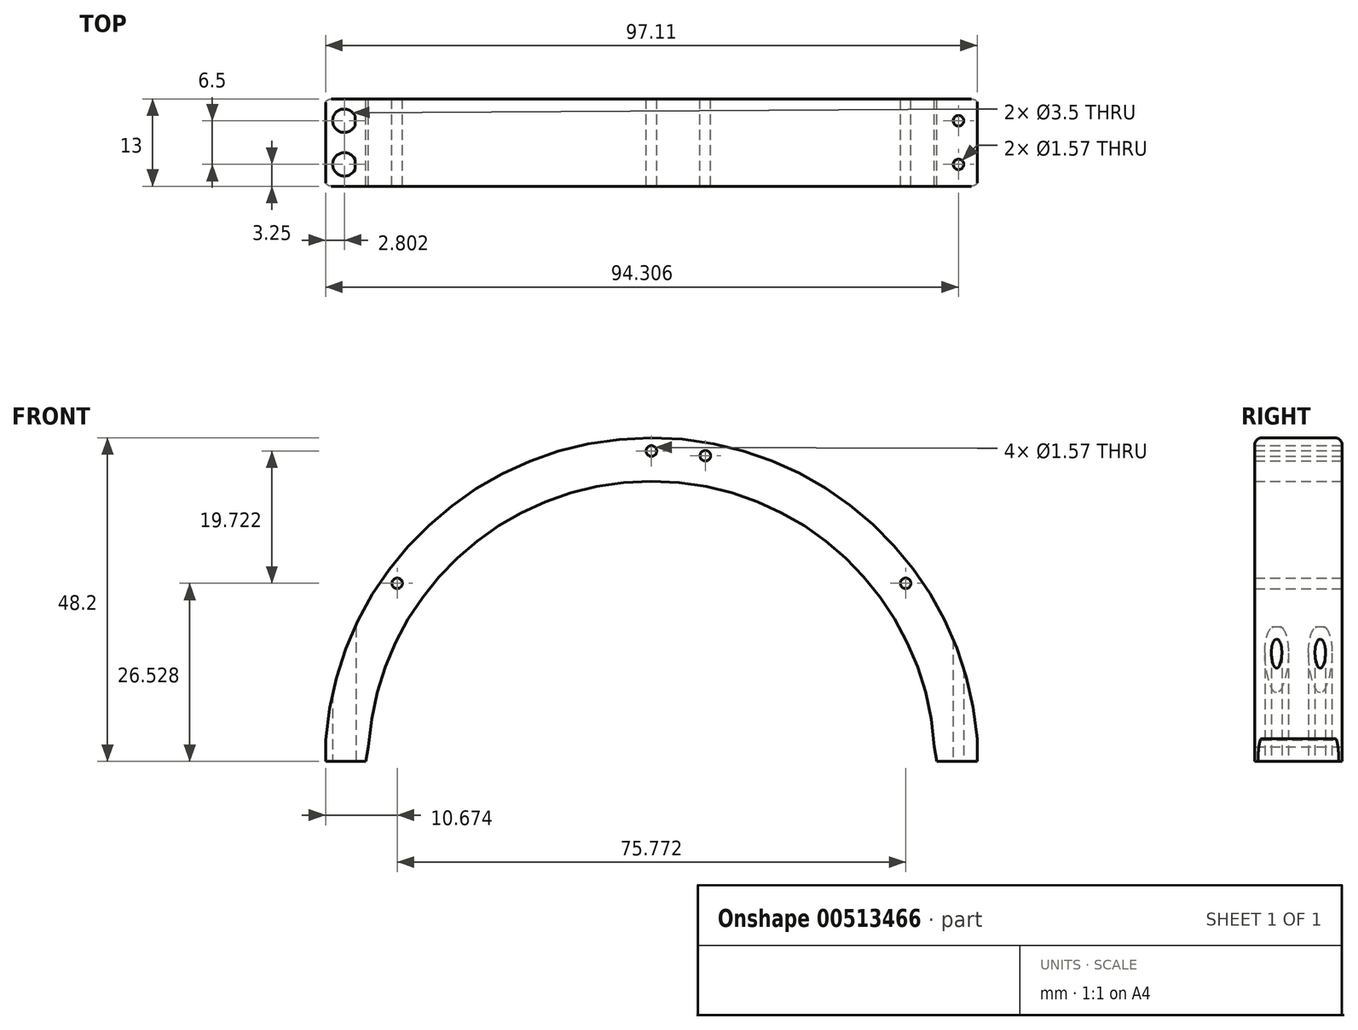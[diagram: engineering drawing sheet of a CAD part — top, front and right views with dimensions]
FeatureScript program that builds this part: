
annotation { "Feature Type Name" : "Feature", "Feature Type Description" : "" }
export const myFeature = defineFeature(function(context is Context, id is Id, definition is map)
    precondition{}
    {
        {
            var Q0;
            Q0=qCreatedBy(makeId("Front.planeOp"),FACE);
            var sketch = newSketch(context, id + "F0", { "sketchPlane" : qUnion([Q0])});
            skLineSegment(sketch, "E0", {"start": v(0, 0) * mm, "end": v(0, 0.5) * mm, "construction": true});
            skLineSegment(sketch, "E1", {"start": v(-42.56, 0.5) * mm, "end": v(-42.56, 2.7) * mm, "construction": true});
            skLineSegment(sketch, "E2", {"start": v(-42.56, 2.7) * mm, "end": v(-34.87, 2.7) * mm, "construction": true});
            skLineSegment(sketch, "E3", {"start": v(-42.56, 0.5) * mm, "end": v(-42.16, 2.7) * mm});
            skLineSegment(sketch, "E4", {"start": v(-42.56, 0.5) * mm, "end": v(0, 0.5) * mm});
            skLineSegment(sketch, "E5.MirrorCS", {"start": v(0.75, 0.5) * mm, "end": v(53.2, 0.5) * mm, "construction": true});
            skLineSegment(sketch, "E6.MirrorCS", {"start": v(-0.5, 0.52) * mm, "end": v(51.96, 0.52) * mm, "construction": true});
            skLineSegment(sketch, "E7", {"start": v(42.05, 0.52) * mm, "end": v(46.75, 0.52) * mm});
            skArc(sketch, "E8", {"start": v(46.25, 0.5) * mm, "mid": v(0, 46.75) * mm, "end": v(-46.25, 0.5) * mm, "construction": true});
            skCircle(sketch, "E9", {"center": v(0, 46.75) * mm, "radius": 1 * mm, "construction": true});
            skLineSegment(sketch, "E10", {"start": v(0, 0.5) * mm, "end": v(9.87, 56.47) * mm, "construction": true});
            skCircle(sketch, "E11", {"center": v(8.03, 46.05) * mm, "radius": 1 * mm, "construction": true});
            skCircle(sketch, "E12", {"center": v(0, 46.75) * mm, "radius": 0.79 * mm, "construction": true});
            skLineSegment(sketch, "E13", {"start": v(0, 0.5) * mm, "end": v(47.68, 33.89) * mm, "construction": true});
            skLineSegment(sketch, "E14", {"start": v(0, 0.5) * mm, "end": v(-44.62, 31.75) * mm, "construction": true});
            skArc(sketch, "E15", {"start": v(42.16, 2.69) * mm, "mid": v(0, 42.25) * mm, "end": v(-42.16, 2.7) * mm});
            skPoint(sketch, "E16.trimOffspring.end.orphan", {"position": v(48.55, 3.87) * mm});
            skArc(sketch, "E17", {"start": v(48.55, 3.87) * mm, "mid": v(-0.08, 48.7) * mm, "end": v(-48.56, 3.71) * mm});
            skLineSegment(sketch, "E18", {"start": v(0, 0) * mm, "end": v(0, 68.97) * mm, "construction": true});
            skPoint(sketch, "E18.endSnap0", {"position": v(0, 0.25) * mm});
            skCircle(sketch, "E19", {"center": v(8.03, 46.05) * mm, "radius": 0.79 * mm, "construction": true});
            skCircle(sketch, "E20", {"center": v(-37.89, 27.03) * mm, "radius": 1 * mm, "construction": true});
            skCircle(sketch, "E21", {"center": v(-37.89, 27.03) * mm, "radius": 0.79 * mm, "construction": true});
            skCircle(sketch, "E22", {"center": v(37.89, 27.03) * mm, "radius": 0.79 * mm, "construction": true});
            skCircle(sketch, "E23", {"center": v(37.89, 27.03) * mm, "radius": 1 * mm, "construction": true});
            skLineSegment(sketch, "E24", {"start": v(48.55, 3.87) * mm, "end": v(48.55, 0.52) * mm});
            skLineSegment(sketch, "E25", {"start": v(48.55, 0.52) * mm, "end": v(46.75, 0.52) * mm});
            skLineSegment(sketch, "E26", {"start": v(-48.56, 3.71) * mm, "end": v(-48.56, 0.5) * mm});
            skLineSegment(sketch, "E27", {"start": v(-42.56, 0.5) * mm, "end": v(-48.56, 0.5) * mm});
            skLineSegment(sketch, "E28.MirrorCS", {"start": v(42.56, 0.5) * mm, "end": v(42.16, 2.7) * mm});
            skSolve(sketch);
        }
        {
            var Q0;
            Q0=makeQuery(id+"F0.imprint","IMPRINT",FACE,{"disambiguationData":[TD([[makeQuery(id+"F0.imprint","IMPRINT",EDGE,{"derivedFrom":sQuery(id+"F0.wireOp",EDGE,"UELqWLm9-NgRF-JSbn-8WNg-CGnTsmN4ftvK")}),1.0]])]});
            var Q1;
            Q1=makeQuery(id+"F0.imprint","IMPRINT",FACE,{"disambiguationData":[TD([[makeQuery(id+"F0.imprint","IMPRINT",EDGE,{"derivedFrom":sQuery(id+"F0.wireOp",EDGE,"E3")}),1.0]])]});
            extrude(context, id + "F1", {"entities" : qUnion([Q0, Q1]), "depth" : 13 * mm, "offsetDistance" : 25 * mm});
        }
        {
            var Q0;
            Q0=sQuery(id+"F0.wireOp",VERTEX,"E9.center");
            var Q1;
            Q1=sQuery(id+"F0.wireOp",VERTEX,"E19.center");
            var Q2;
            Q2=sQuery(id+"F0.wireOp",VERTEX,"E23.center");
            var Q3;
            Q3=sQuery(id+"F0.wireOp",VERTEX,"E21.center");
            var Q4;
            Q4=makeQuery(id+"F1.opExtrude","SWEPT_BODY",BODY,{"disambiguationData":[OSD([sQuery(id+"F0.wireOp",EDGE,"UELqWLm9-NgRF-JSbn-8WNg-CGnTsmN4ftvK"),sQuery(id+"F0.wireOp",EDGE,"zs116KGF-nC6e-KLYb-P88h-iOdVpbJrE8ox"),sQuery(id+"F0.wireOp",EDGE,"E3"),sQuery(id+"F0.wireOp",EDGE,"92af82e9-8861-4be0-b8ea-6b4333b21a260.MirrorCS"),sQuery(id+"F0.wireOp",EDGE,"35d9bae8-f3c6-4467-bb19-02aff46f1e0d0.MirrorCS"),sQuery(id+"F0.wireOp",EDGE,"E7"),sQuery(id+"F0.wireOp",EDGE,"E9"),sQuery(id+"F0.wireOp",EDGE,"E11"),sQuery(id+"F0.wireOp",EDGE,"E15"),sQuery(id+"F0.wireOp",EDGE,"E17"),sQuery(id+"F0.wireOp",EDGE,"E23")])]});
            hole(context, id + "F2", {"style" : HoleStyle.SIMPLE, "endStyle" : HoleEndStyle.BLIND, "oppositeDirection" : true, "holeDiameter" : 1.57 * mm, "holeDepth" : 14.5 * mm, "isTappedThrough" : true, "tappedDepth" : 12 * mm, "tapClearance" : 3, "locations" : qUnion([Q0, Q1, Q2, Q3]), "scope" : qUnion([Q4])});
        }
        {
            var Q0;
            Q0=makeQuery(id+"F1.opExtrude","SWEPT_FACE",FACE,{"disambiguationData":[OSD([sQuery(id+"F0.wireOp",EDGE,"E27")])]});
            var sketch = newSketch(context, id + "F3", { "sketchPlane" : qUnion([Q0])});
            skLineSegment(sketch, "E29.0", {"start": v(-45.76, 14.5) * mm, "end": v(-45.76, 0) * mm, "construction": true});
            skLineSegment(sketch, "E30.0", {"start": v(-42.56, 9.75) * mm, "end": v(-48.36, 9.75) * mm, "construction": true});
            skLineSegment(sketch, "E31.0", {"start": v(-42.56, 3.25) * mm, "end": v(-48.36, 3.25) * mm, "construction": true});
            skCircle(sketch, "E32", {"center": v(-45.76, 9.75) * mm, "radius": 0.48 * mm});
            skCircle(sketch, "E33", {"center": v(-45.76, 3.25) * mm, "radius": 0.56 * mm});
            skSolve(sketch);
        }
        {
            var Q0;
            Q0=sQuery(id+"F3.wireOp",VERTEX,"E32.center");
            var Q1;
            Q1=sQuery(id+"F3.wireOp",VERTEX,"E33.center");
            var Q2;
            Q2=makeQuery(id+"F1.opExtrude","SWEPT_BODY",BODY,{"disambiguationData":[OSD([sQuery(id+"F0.wireOp",EDGE,"E3"),sQuery(id+"F0.wireOp",EDGE,"E7"),sQuery(id+"F0.wireOp",EDGE,"E15"),sQuery(id+"F0.wireOp",EDGE,"E17"),sQuery(id+"F0.wireOp",EDGE,"E24"),sQuery(id+"F0.wireOp",EDGE,"E25"),sQuery(id+"F0.wireOp",EDGE,"E26"),sQuery(id+"F0.wireOp",EDGE,"E27"),sQuery(id+"F0.wireOp",EDGE,"E28.MirrorCS")])]});
            hole(context, id + "F4", {"style" : HoleStyle.SIMPLE, "endStyle" : HoleEndStyle.BLIND, "holeDiameter" : 3.5 * mm, "holeDepth" : 20 * mm, "isTappedThrough" : true, "tappedDepth" : 12 * mm, "tapClearance" : 3, "locations" : qUnion([Q0, Q1]), "scope" : qUnion([Q2])});
        }
        {
            var Q0;
            Q0=makeQuery(id+"F1.opExtrude","SWEPT_FACE",FACE,{"disambiguationData":[OSD([sQuery(id+"F0.wireOp",EDGE,"E7"),sQuery(id+"F0.wireOp",EDGE,"E25")])]});
            var sketch = newSketch(context, id + "F5", { "sketchPlane" : qUnion([Q0])});
            skLineSegment(sketch, "E34.0", {"start": v(45.75, 14.5) * mm, "end": v(45.75, 0) * mm, "construction": true});
            skLineSegment(sketch, "E35.0", {"start": v(42.56, 9.75) * mm, "end": v(48.35, 9.75) * mm, "construction": true});
            skLineSegment(sketch, "E36.0", {"start": v(41.85, 3.25) * mm, "end": v(46.55, 3.25) * mm, "construction": true});
            skCircle(sketch, "E37", {"center": v(45.75, 3.25) * mm, "radius": 0.82 * mm});
            skCircle(sketch, "E38", {"center": v(45.75, 9.75) * mm, "radius": 0.6 * mm});
            skSolve(sketch);
        }
        {
            var Q0;
            Q0=sQuery(id+"F5.wireOp",VERTEX,"E37.center");
            var Q1;
            Q1=sQuery(id+"F5.wireOp",VERTEX,"E38.center");
            var Q2;
            Q2=makeQuery(id+"F1.opExtrude","SWEPT_BODY",BODY,{"disambiguationData":[OSD([sQuery(id+"F0.wireOp",EDGE,"E3"),sQuery(id+"F0.wireOp",EDGE,"E7"),sQuery(id+"F0.wireOp",EDGE,"E15"),sQuery(id+"F0.wireOp",EDGE,"E17"),sQuery(id+"F0.wireOp",EDGE,"E24"),sQuery(id+"F0.wireOp",EDGE,"E25"),sQuery(id+"F0.wireOp",EDGE,"E26"),sQuery(id+"F0.wireOp",EDGE,"E27"),sQuery(id+"F0.wireOp",EDGE,"E28.MirrorCS")])]});
            hole(context, id + "F6", {"style" : HoleStyle.SIMPLE, "endStyle" : HoleEndStyle.BLIND, "holeDiameter" : 1.57 * mm, "holeDepth" : 20 * mm, "isTappedThrough" : true, "tappedDepth" : 12 * mm, "tapClearance" : 3, "locations" : qUnion([Q0, Q1]), "scope" : qUnion([Q2])});
        }
        {
            var Q0;
            Q0=makeQuery(id+"F1.opExtrude","CAP_EDGE",EDGE,{"disambiguationData":[OSD([sQuery(id+"F0.wireOp",EDGE,"E17")])],"isStart":false});
            var Q1;
            Q1=makeQuery(id+"F1.opExtrude","CAP_EDGE",EDGE,{"disambiguationData":[OSD([sQuery(id+"F0.wireOp",EDGE,"E17")])],"isStart":true});
            fillet(context, id + "F7", {"entities" : qUnion([Q0, Q1]), "radius" : 1 * mm, "tangentPropagation" : true, "allowEdgeOverflow" : false});
        }
    });
